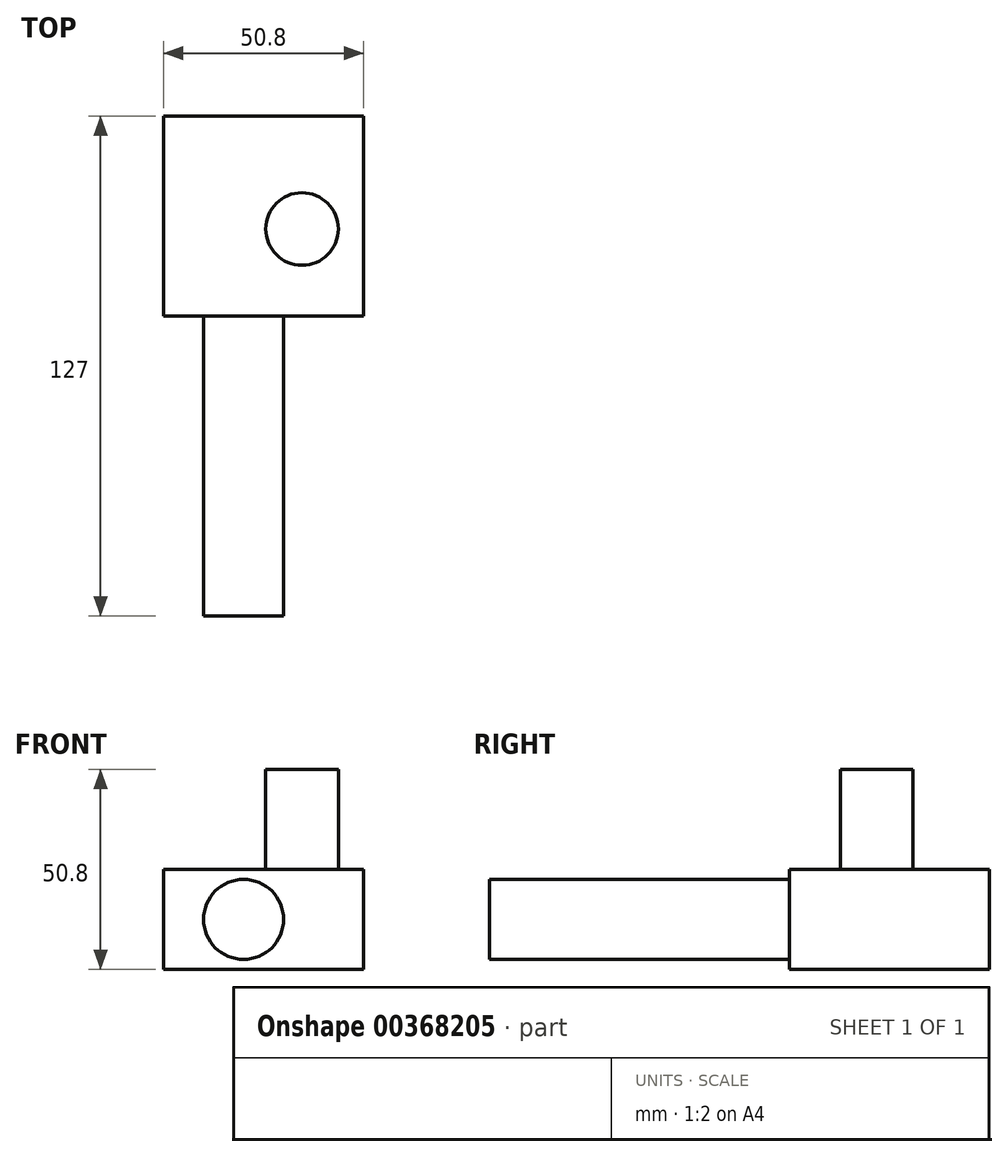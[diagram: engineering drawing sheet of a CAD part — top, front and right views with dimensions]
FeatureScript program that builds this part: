
annotation { "Feature Type Name" : "Feature", "Feature Type Description" : "" }
export const myFeature = defineFeature(function(context is Context, id is Id, definition is map)
    precondition{}
    {
        {
            var Q0;
            Q0=qCreatedBy(makeId("Top.planeOp"),FACE);
            var sketch = newSketch(context, id + "F0", { "sketchPlane" : qUnion([Q0])});
            skLineSegment(sketch, "E0.bottom", {"start": v(0, 0) * mm, "end": v(50.8, 0) * mm});
            skLineSegment(sketch, "E0.top", {"start": v(0, 50.8) * mm, "end": v(50.8, 50.8) * mm});
            skLineSegment(sketch, "E0.left", {"start": v(0, 0) * mm, "end": v(0, 50.8) * mm});
            skLineSegment(sketch, "E0.right", {"start": v(50.8, 0) * mm, "end": v(50.8, 50.8) * mm});
            skSolve(sketch);
        }
        {
            var Q0;
            Q0=makeQuery(id+"F0.imprint","IMPRINT",FACE,{"disambiguationData":[TD([[makeQuery(id+"F0.imprint","IMPRINT",EDGE,{"derivedFrom":sQuery(id+"F0.wireOp",EDGE,"E0.bottom")}),1.0]])]});
            extrude(context, id + "F1", {"entities" : qUnion([Q0]), "depth" : 25.4 * mm});
        }
        {
            var Q0;
            Q0=makeQuery(id+"F1.opExtrude","SWEPT_FACE",FACE,{"disambiguationData":[OSD([sQuery(id+"F0.wireOp",EDGE,"E0.bottom")])]});
            var sketch = newSketch(context, id + "F2", { "sketchPlane" : qUnion([Q0])});
            skCircle(sketch, "E1", {"center": v(20.32, 12.7) * mm, "radius": 10.16 * mm});
            skSolve(sketch);
        }
        {
            var Q0;
            Q0=makeQuery(id+"F2.imprint","IMPRINT",FACE,{"disambiguationData":[TD([[makeQuery(id+"F2.imprint","IMPRINT",EDGE,{"derivedFrom":sQuery(id+"F2.wireOp",EDGE,"E1")}),1.0]])]});
            extrude(context, id + "F3", {"entities" : qUnion([Q0]), "operationType" : NewBodyOperationType.ADD, "depth" : 76.2 * mm});
        }
        {
            var Q0;
            Q0=makeQuery(id+"F1.opExtrude","CAP_FACE",FACE,{"disambiguationData":[OSD([sQuery(id+"F0.wireOp",EDGE,"E0.bottom"),sQuery(id+"F0.wireOp",EDGE,"E0.top"),sQuery(id+"F0.wireOp",EDGE,"E0.left"),sQuery(id+"F0.wireOp",EDGE,"E0.right")])],"isStart":false});
            var sketch = newSketch(context, id + "F4", { "sketchPlane" : qUnion([Q0])});
            skCircle(sketch, "E2", {"center": v(35.16, 22.12) * mm, "radius": 9.22 * mm});
            skSolve(sketch);
        }
        {
            var Q0;
            Q0=makeQuery(id+"F4.imprint","IMPRINT",FACE,{"disambiguationData":[TD([[makeQuery(id+"F4.imprint","IMPRINT",EDGE,{"derivedFrom":sQuery(id+"F4.wireOp",EDGE,"E2")}),1.0]])]});
            extrude(context, id + "F5", {"entities" : qUnion([Q0]), "operationType" : NewBodyOperationType.ADD, "depth" : 25.4 * mm});
        }
    });
